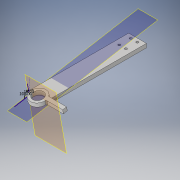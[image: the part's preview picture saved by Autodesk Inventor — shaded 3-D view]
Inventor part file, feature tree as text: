
AUTODESK INVENTOR PART (.ipt)
format: ipt  version: 2017 (Build 210142000, 142)  size: 171,520 bytes
history: native  units: in
note: dims shown in document units (in); Inventor stores cm internally (conversion verified against a paired STEP export)
features: projected_geometry x6, sketch x5, extrude x3, plane x2, hole x2
ambient origin geometry x8: Origin, YZ Plane, XZ Plane, XY Plane, X Axis, Y Axis, Z Axis, Center Point
bodies: Solid1 (feature_tree)
feature tree (18):
  extrude  "Extrusion1"  Depth=4.757in
  sketch  "Sketch2"  dims[d2=0.1875in d3=0.0in d4=0.6871in]
  plane  "Work Plane1"
  extrude  "Extrusion2"  Depth=0.1875in
  plane  "Work Plane3"
  hole  "Hole3"  [1 undecoded]
  hole  "Hole4"  [1 undecoded]
  extrude  "Extrusion5"  Depth=0.1875in
  sketch  "Sketch1"  dims[d0=0.85in d1=4.757in]
  projected_geometry  "Projected Loop1"
  projected_geometry  "Projected Loop2"
  sketch  "Sketch9"  dims[d6=0.85in d8=0.1875in d9=0.0in]
  projected_geometry  "Projected Loop10"
  sketch  "Sketch11"  dims[d24=0.0687in d25=90.0deg]
  projected_geometry  "Projected Loop12"
  sketch  "Sketch12"  dims[d34=0.6299in d35=0.315in d36=0.1575in d37=0.85in d38=0.425in d39=0.44in d40=0.11in d41=0.75in d42=0.375in d43=0.25in d44=0.5635in d45=1.0in d46=0.8108in d50=0.75in d51=0.034in d52=0.505in d53=0.75in d54=0.375in d55=0.25in d56=0.5635in d57=1.0in d58=0.8108in d59=0.1875in d60=0.926in d61=0.1875in d62=0.0in]
  projected_geometry  "Projected Loop13"
  projected_geometry  "Projected Loop14"
note: 2 required parameter values undecoded (feature->parameter linkage not recoverable at this tier; creation-order binding heuristic only, values carry confidence <= 0.55)
